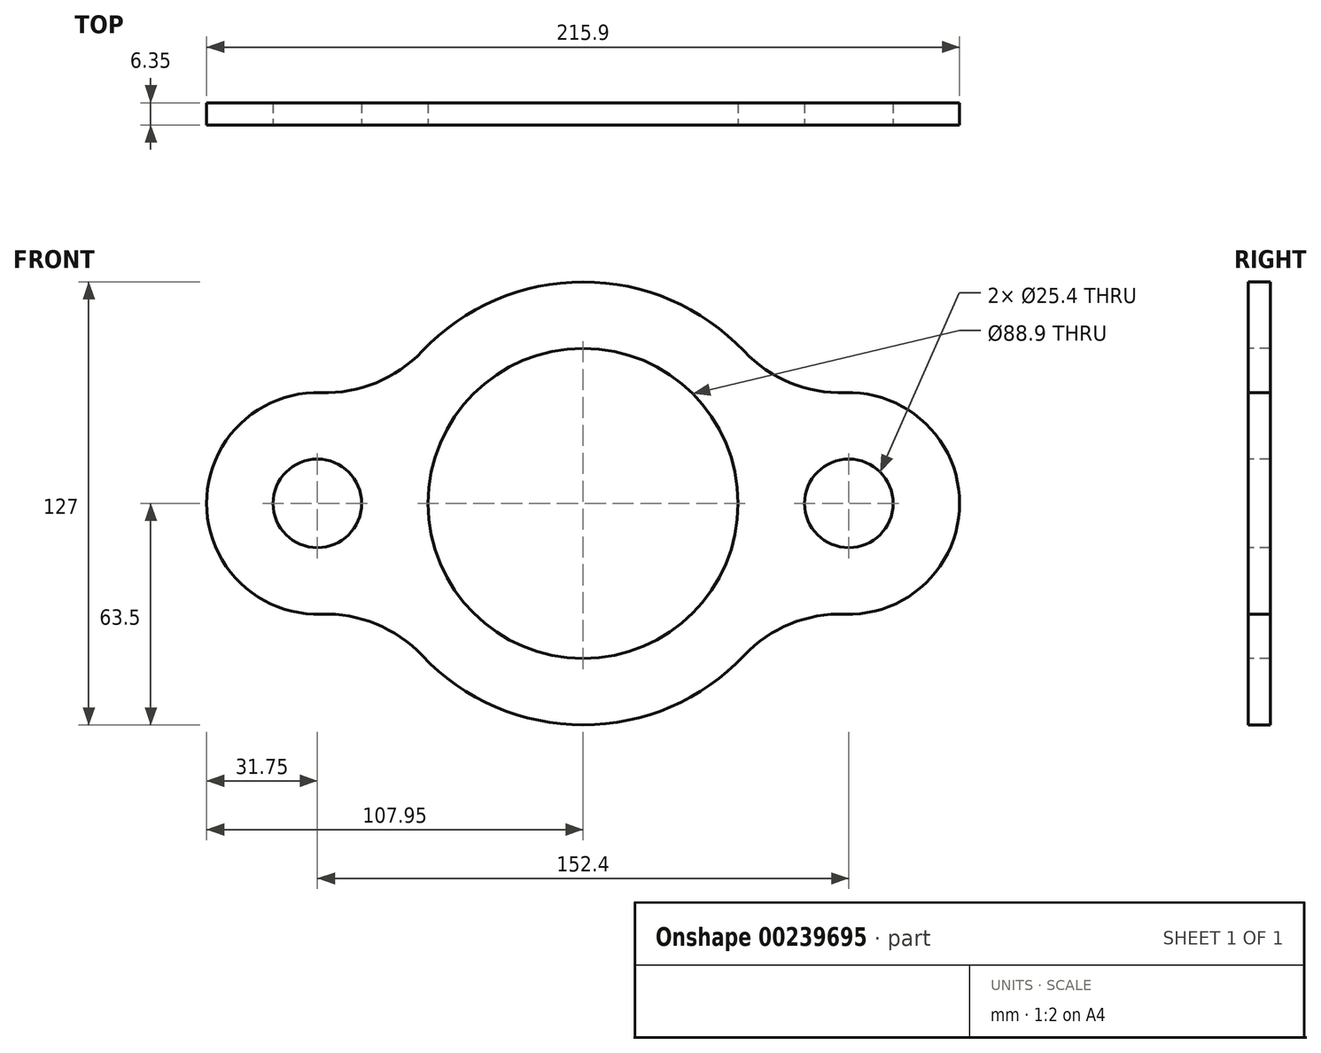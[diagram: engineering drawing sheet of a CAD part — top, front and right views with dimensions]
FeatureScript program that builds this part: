
annotation { "Feature Type Name" : "Feature", "Feature Type Description" : "" }
export const myFeature = defineFeature(function(context is Context, id is Id, definition is map)
    precondition{}
    {
        {
            var Q0;
            Q0=qCreatedBy(makeId("Front.planeOp"),FACE);
            var sketch = newSketch(context, id + "F0", { "sketchPlane" : qUnion([Q0])});
            skLineSegment(sketch, "E0", {"start": v(-76.2, 0) * mm, "end": v(76.2, 0) * mm, "construction": true});
            skLineSegment(sketch, "E1", {"start": v(0, 97.25) * mm, "end": v(0, -97.25) * mm, "construction": true});
            skCircle(sketch, "E2", {"center": v(-76.2, 0) * mm, "radius": 12.7 * mm});
            skCircle(sketch, "E3", {"center": v(76.2, 0) * mm, "radius": 12.7 * mm});
            skCircle(sketch, "E4", {"center": v(0, 0) * mm, "radius": 44.45 * mm});
            skLineSegment(sketch, "E5", {"start": v(-76.2, 75.47) * mm, "end": v(-76.2, -84.84) * mm, "construction": true});
            skLineSegment(sketch, "E6", {"start": v(76.2, 75.48) * mm, "end": v(76.2, -84.84) * mm, "construction": true});
            skArc(sketch, "E7", {"start": v(46.14, 43.63) * mm, "mid": v(0, 63.5) * mm, "end": v(-46.14, 43.63) * mm});
            skArc(sketch, "E8", {"start": v(75.12, -31.73) * mm, "mid": v(107.95, 0) * mm, "end": v(75.12, 31.73) * mm});
            skArc(sketch, "E9.filletArc", {"start": v(46.14, 43.63) * mm, "mid": v(59.35, 34.56) * mm, "end": v(75.12, 31.73) * mm});
            skArc(sketch, "E10", {"start": v(-75.12, 31.73) * mm, "mid": v(-107.95, 0) * mm, "end": v(-75.12, -31.73) * mm});
            skArc(sketch, "E11", {"start": v(-46.14, -43.63) * mm, "mid": v(0, -63.5) * mm, "end": v(46.14, -43.63) * mm});
            skArc(sketch, "E12.filletArc", {"start": v(-75.12, 31.73) * mm, "mid": v(-59.35, 34.56) * mm, "end": v(-46.14, 43.63) * mm});
            skArc(sketch, "E13.filletArc", {"start": v(-46.14, -43.63) * mm, "mid": v(-59.35, -34.56) * mm, "end": v(-75.12, -31.73) * mm});
            skArc(sketch, "E14.filletArc", {"start": v(75.12, -31.73) * mm, "mid": v(59.35, -34.56) * mm, "end": v(46.14, -43.63) * mm});
            skSolve(sketch);
        }
        {
            var Q0;
            Q0=makeQuery(id+"F0.imprint","IMPRINT",FACE,{"disambiguationData":[TD([[makeQuery(id+"F0.imprint","IMPRINT",EDGE,{"derivedFrom":sQuery(id+"F0.wireOp",EDGE,"E2")}),-1.0]])]});
            extrude(context, id + "F1", {"entities" : qUnion([Q0]), "oppositeDirection" : true, "depth" : 6.35 * mm});
        }
    });
